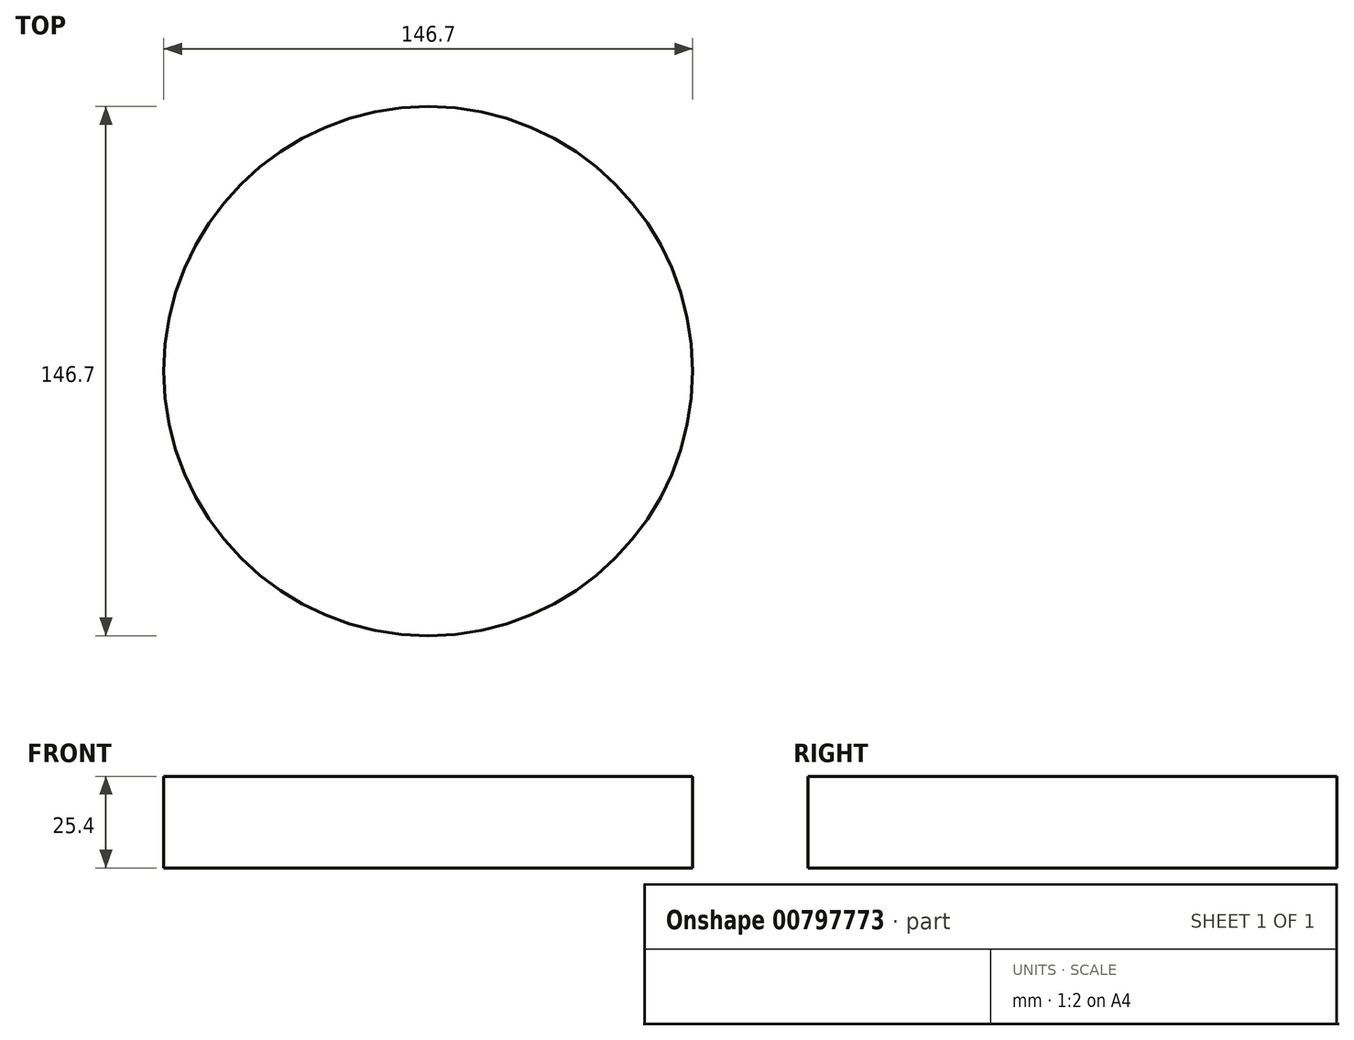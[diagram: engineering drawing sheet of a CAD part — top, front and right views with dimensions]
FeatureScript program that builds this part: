
annotation { "Feature Type Name" : "Feature", "Feature Type Description" : "" }
export const myFeature = defineFeature(function(context is Context, id is Id, definition is map)
    precondition{}
    {
        {
            var Q0;
            Q0=qCreatedBy(makeId("Top.planeOp"),FACE);
            var sketch = newSketch(context, id + "F0", { "sketchPlane" : qUnion([Q0])});
            skCircle(sketch, "E0", {"center": v(0, 0) * mm, "radius": 73.35 * mm});
            skSolve(sketch);
        }
        {
            var Q0;
            Q0 = qSketchRegion(id + "F0", true);
            extrude(context, id + "F1", {"entities" : qUnion([Q0]), "depth" : 25.4 * mm, "offsetDistance" : 25.4 * mm});
        }
    });
